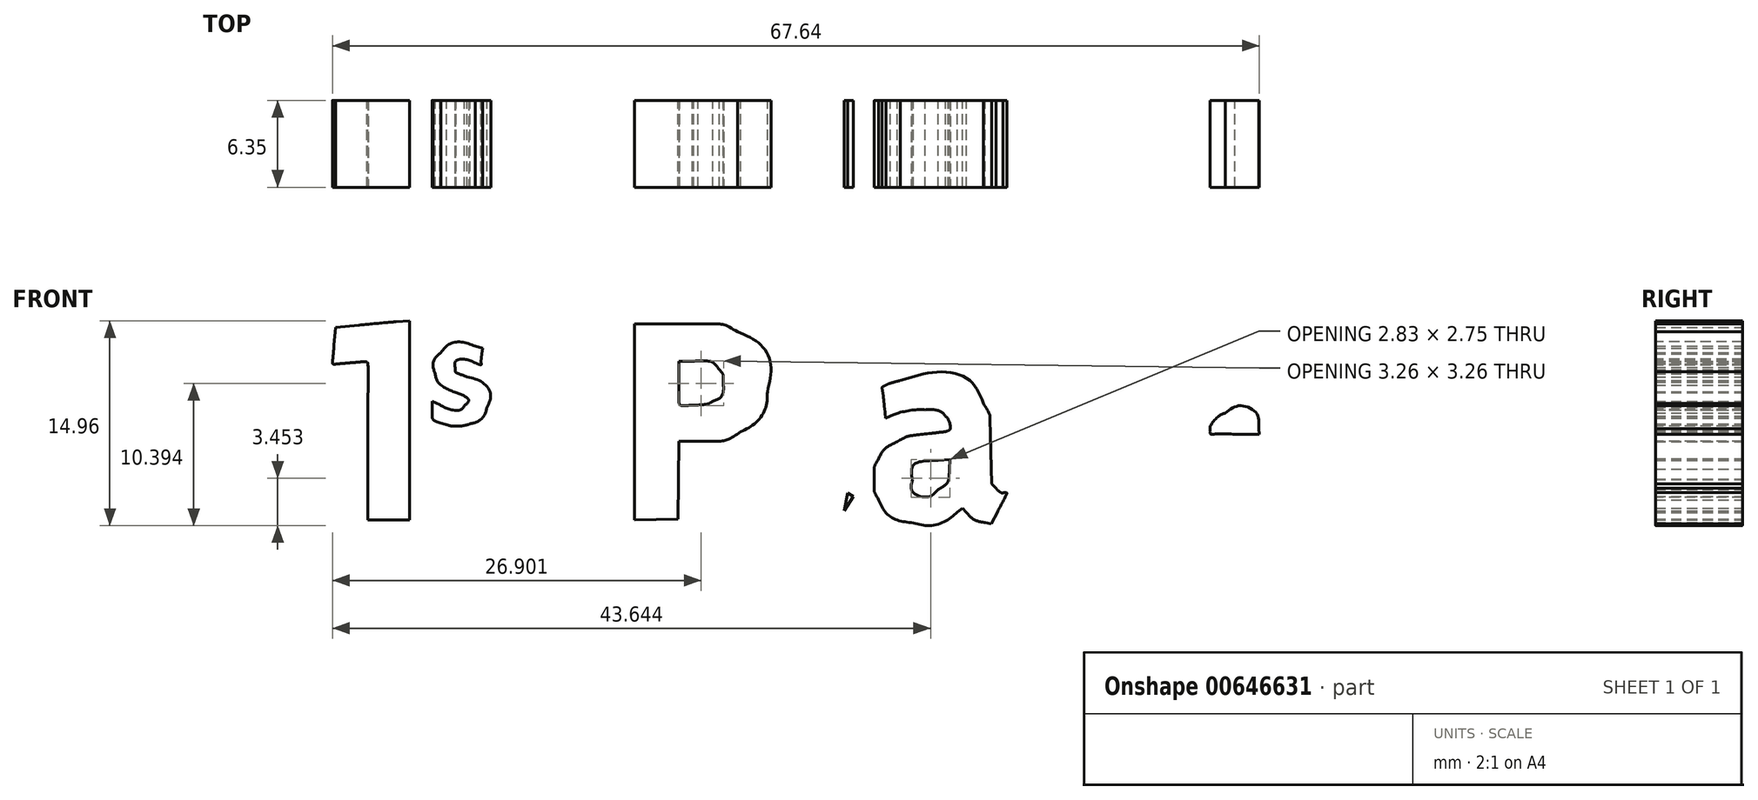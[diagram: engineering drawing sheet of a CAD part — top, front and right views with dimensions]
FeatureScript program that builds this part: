
annotation { "Feature Type Name" : "Feature", "Feature Type Description" : "" }
export const myFeature = defineFeature(function(context is Context, id is Id, definition is map)
    precondition{}
    {
        {
            var Q0;
            Q0=qCreatedBy(makeId("Front.planeOp"),FACE);
            var sketch = newSketch(context, id + "F0", { "sketchPlane" : qUnion([Q0])});
            skFitSpline(sketch, "E0", {"points": [v(0.33, -8.9) * mm, v(-0.3, -8.66) * mm, v(-0.98, -8.12) * mm, v(-1.33, -7.57) * mm]});
            skFitSpline(sketch, "E1", {"points": [v(-1.33, -7.57) * mm, v(-1.97, -6.57) * mm, v(-1.96, -6.72) * mm, v(-1.96, 0.66) * mm]});
            skFitSpline(sketch, "E2", {"points": [v(1.12, 0.8) * mm, v(1.12, -6.54) * mm, v(1.08, -6.16) * mm, v(1.9, -6.65) * mm]});
            skFitSpline(sketch, "E3", {"points": [v(1.64, -7.94) * mm, v(1.27, -8.51) * mm, v(0.9, -9) * mm, v(0.84, -9) * mm]});
            skFitSpline(sketch, "E4", {"points": [v(0.84, -9) * mm, v(0.76, -9.02) * mm, v(0.54, -8.97) * mm, v(0.33, -8.9) * mm]});
            skLineSegment(sketch, "E5", {"start": v(1.9, -6.65) * mm, "end": v(2.3, -6.9) * mm});
            skLineSegment(sketch, "E6", {"start": v(2.3, -6.9) * mm, "end": v(1.64, -7.94) * mm});
            skLineSegment(sketch, "E7", {"start": v(1.64, -7.94) * mm, "end": v(1.9, -6.65) * mm});
            skFitSpline(sketch, "E8", {"points": [v(6.68, -8.82) * mm, v(5.5, -8.61) * mm, v(4.66, -8.05) * mm, v(4.15, -7.14) * mm]});
            skFitSpline(sketch, "E9", {"points": [v(4.15, -7.14) * mm, v(3.87, -6.63) * mm, v(3.84, -6.48) * mm, v(3.84, -5.63) * mm]});
            skFitSpline(sketch, "E10", {"points": [v(3.84, -5.63) * mm, v(3.84, -4.8) * mm, v(3.87, -4.64) * mm, v(4.15, -4.14) * mm]});
            skFitSpline(sketch, "E11", {"points": [v(4.15, -4.14) * mm, v(4.46, -3.57) * mm, v(4.8, -3.26) * mm, v(5.51, -2.9) * mm]});
            skFitSpline(sketch, "E12", {"points": [v(5.51, -2.9) * mm, v(6.22, -2.53) * mm, v(6.51, -2.45) * mm, v(7.83, -2.3) * mm]});
            skFitSpline(sketch, "E13", {"points": [v(7.83, -2.3) * mm, v(8.53, -2.22) * mm, v(9.16, -2.12) * mm, v(9.22, -2.08) * mm]});
            skFitSpline(sketch, "E14", {"points": [v(9.22, -2.08) * mm, v(9.38, -1.99) * mm, v(9.25, -1.3) * mm, v(9.03, -1.05) * mm]});
            skFitSpline(sketch, "E15", {"points": [v(9.03, -1.05) * mm, v(8.76, -0.73) * mm, v(8.24, -0.56) * mm, v(7.55, -0.56) * mm]});
            skFitSpline(sketch, "E16", {"points": [v(7.55, -0.56) * mm, v(6.85, -0.56) * mm, v(5.57, -0.8) * mm, v(5, -1.03) * mm]});
            skFitSpline(sketch, "E17", {"points": [v(4.58, -0.43) * mm, v(4.54, -0.01) * mm, v(4.49, 0.5) * mm, v(4.46, 0.71) * mm]});
            skFitSpline(sketch, "E18", {"points": [v(4.46, 0.71) * mm, v(4.4, 1.05) * mm, v(4.43, 1.11) * mm, v(4.7, 1.25) * mm]});
            skFitSpline(sketch, "E19", {"points": [v(4.7, 1.25) * mm, v(4.86, 1.33) * mm, v(5.33, 1.47) * mm, v(5.75, 1.57) * mm]});
            skFitSpline(sketch, "E20", {"points": [v(5.75, 1.57) * mm, v(8.56, 2.2) * mm, v(10.81, 1.58) * mm, v(11.8, -0.1) * mm]});
            skFitSpline(sketch, "E21", {"points": [v(11.8, -0.1) * mm, v(12.23, -0.83) * mm, v(12.28, -1.14) * mm, v(12.35, -3.61) * mm]});
            skLineSegment(sketch, "E22", {"start": v(5, -1.03) * mm, "end": v(4.65, -1.18) * mm});
            skLineSegment(sketch, "E23", {"start": v(4.65, -1.18) * mm, "end": v(4.58, -0.43) * mm});
            skFitSpline(sketch, "E24", {"points": [v(12.72, -6.3) * mm, v(12.9, -6.48) * mm, v(13.12, -6.63) * mm, v(13.23, -6.63) * mm]});
            skFitSpline(sketch, "E25", {"points": [v(13.23, -6.63) * mm, v(13.5, -6.63) * mm, v(13.43, -6.86) * mm, v(12.84, -8) * mm]});
            skLineSegment(sketch, "E26", {"start": v(12.35, -3.61) * mm, "end": v(12.42, -5.99) * mm});
            skLineSegment(sketch, "E27", {"start": v(12.42, -5.99) * mm, "end": v(12.72, -6.3) * mm});
            skFitSpline(sketch, "E28", {"points": [v(11.93, -8.8) * mm, v(11.35, -8.68) * mm, v(10.92, -8.44) * mm, v(10.58, -8.06) * mm]});
            skLineSegment(sketch, "E29", {"start": v(12.84, -8) * mm, "end": v(12.36, -8.9) * mm});
            skLineSegment(sketch, "E30", {"start": v(12.36, -8.9) * mm, "end": v(11.93, -8.8) * mm});
            skFitSpline(sketch, "E31", {"points": [v(9.91, -8.03) * mm, v(9, -8.72) * mm, v(7.78, -9.02) * mm, v(6.68, -8.82) * mm]});
            skLineSegment(sketch, "E32", {"start": v(10.58, -8.06) * mm, "end": v(10.28, -7.74) * mm});
            skLineSegment(sketch, "E33", {"start": v(10.28, -7.74) * mm, "end": v(9.91, -8.03) * mm});
            skFitSpline(sketch, "E34", {"points": [v(8.5, -6.4) * mm, v(9.08, -6) * mm, v(9.26, -5.65) * mm, v(9.31, -4.88) * mm]});
            skFitSpline(sketch, "E35", {"points": [v(8.49, -4.26) * mm, v(7.1, -4.38) * mm, v(6.61, -4.74) * mm, v(6.61, -5.67) * mm]});
            skFitSpline(sketch, "E36", {"points": [v(6.61, -5.67) * mm, v(6.61, -6.52) * mm, v(7.7, -6.93) * mm, v(8.5, -6.4) * mm]});
            skLineSegment(sketch, "E37", {"start": v(9.31, -4.88) * mm, "end": v(9.36, -4.2) * mm});
            skLineSegment(sketch, "E38", {"start": v(9.36, -4.2) * mm, "end": v(8.49, -4.26) * mm});
            skFitSpline(sketch, "E39", {"points": [v(19.3, -8.81) * mm, v(18.14, -8.62) * mm, v(16.94, -7.97) * mm, v(16.1, -7.07) * mm]});
            skFitSpline(sketch, "E40", {"points": [v(16.1, -7.07) * mm, v(14.63, -5.48) * mm, v(14.33, -3.05) * mm, v(15.38, -1.04) * mm]});
            skFitSpline(sketch, "E41", {"points": [v(15.38, -1.04) * mm, v(16.6, 1.31) * mm, v(19.52, 2.37) * mm, v(22.46, 1.53) * mm]});
            skFitSpline(sketch, "E42", {"points": [v(22.46, 1.53) * mm, v(23.5, 1.23) * mm, v(23.5, 1.24) * mm, v(23.37, -0.19) * mm]});
            skFitSpline(sketch, "E43", {"points": [v(23.37, -0.19) * mm, v(23.32, -0.85) * mm, v(23.25, -1.42) * mm, v(23.22, -1.45) * mm]});
            skFitSpline(sketch, "E44", {"points": [v(23.22, -1.45) * mm, v(23.19, -1.48) * mm, v(22.93, -1.4) * mm, v(22.65, -1.28) * mm]});
            skFitSpline(sketch, "E45", {"points": [v(22.65, -1.28) * mm, v(22.28, -1.11) * mm, v(21.87, -1.03) * mm, v(21.17, -1) * mm]});
            skFitSpline(sketch, "E46", {"points": [v(21.17, -1) * mm, v(19.85, -0.94) * mm, v(19.36, -1.09) * mm, v(18.68, -1.76) * mm]});
            skFitSpline(sketch, "E47", {"points": [v(18.68, -1.76) * mm, v(18.21, -2.21) * mm, v(18.12, -2.38) * mm, v(18.01, -2.9) * mm]});
            skFitSpline(sketch, "E48", {"points": [v(18.01, -2.9) * mm, v(17.8, -3.92) * mm, v(18, -4.62) * mm, v(18.7, -5.28) * mm]});
            skFitSpline(sketch, "E49", {"points": [v(18.7, -5.28) * mm, v(19.43, -5.97) * mm, v(19.69, -6.05) * mm, v(21.1, -6.05) * mm]});
            skFitSpline(sketch, "E50", {"points": [v(21.1, -6.05) * mm, v(22.17, -6.05) * mm, v(22.42, -6.02) * mm, v(22.86, -5.82) * mm]});
            skFitSpline(sketch, "E51", {"points": [v(23.3, -6.44) * mm, v(23.26, -6.92) * mm, v(23.2, -7.55) * mm, v(23.17, -7.85) * mm]});
            skLineSegment(sketch, "E52", {"start": v(22.86, -5.82) * mm, "end": v(23.37, -5.58) * mm});
            skLineSegment(sketch, "E53", {"start": v(23.37, -5.58) * mm, "end": v(23.3, -6.44) * mm});
            skFitSpline(sketch, "E54", {"points": [v(22.54, -8.56) * mm, v(21.5, -8.9) * mm, v(20.31, -8.98) * mm, v(19.3, -8.81) * mm]});
            skLineSegment(sketch, "E55", {"start": v(23.17, -7.85) * mm, "end": v(23.1, -8.38) * mm});
            skLineSegment(sketch, "E56", {"start": v(23.1, -8.38) * mm, "end": v(22.54, -8.56) * mm});
            skFitSpline(sketch, "E57", {"points": [v(29.9, -8.83) * mm, v(27, -8.3) * mm, v(25.12, -6.2) * mm, v(25.12, -3.5) * mm]});
            skFitSpline(sketch, "E58", {"points": [v(25.12, -3.5) * mm, v(25.12, -1.07) * mm, v(26.47, 0.82) * mm, v(28.78, 1.6) * mm]});
            skFitSpline(sketch, "E59", {"points": [v(28.78, 1.6) * mm, v(29.57, 1.86) * mm, v(31.13, 1.86) * mm, v(31.91, 1.59) * mm]});
            skFitSpline(sketch, "E60", {"points": [v(31.91, 1.59) * mm, v(32.98, 1.22) * mm, v(33.71, 0.67) * mm, v(34.26, -0.2) * mm]});
            skFitSpline(sketch, "E61", {"points": [v(34.26, -0.2) * mm, v(34.7, -0.87) * mm, v(34.84, -1.41) * mm, v(34.84, -2.28) * mm]});
            skFitSpline(sketch, "E62", {"points": [v(30.9, -4.43) * mm, v(28.12, -4.43) * mm, v(28.18, -4.42) * mm, v(28.5, -5.04) * mm]});
            skFitSpline(sketch, "E63", {"points": [v(28.5, -5.04) * mm, v(29.26, -6.48) * mm, v(31.57, -6.94) * mm, v(33.7, -6.07) * mm]});
            skLineSegment(sketch, "E64", {"start": v(34.84, -2.28) * mm, "end": v(34.84, -2.99) * mm});
            skLineSegment(sketch, "E65", {"start": v(34.84, -2.99) * mm, "end": v(34.15, -3.7) * mm});
            skLineSegment(sketch, "E66", {"start": v(34.15, -3.7) * mm, "end": v(33.45, -4.43) * mm});
            skLineSegment(sketch, "E67", {"start": v(33.45, -4.43) * mm, "end": v(30.9, -4.43) * mm});
            skFitSpline(sketch, "E68", {"points": [v(34.14, -7.04) * mm, v(34.06, -7.7) * mm, v(33.96, -8.28) * mm, v(33.9, -8.34) * mm]});
            skFitSpline(sketch, "E69", {"points": [v(33.9, -8.34) * mm, v(33.55, -8.7) * mm, v(30.94, -9.02) * mm, v(29.9, -8.83) * mm]});
            skLineSegment(sketch, "E70", {"start": v(33.7, -6.07) * mm, "end": v(34.28, -5.83) * mm});
            skLineSegment(sketch, "E71", {"start": v(34.28, -5.83) * mm, "end": v(34.14, -7.04) * mm});
            skFitSpline(sketch, "E72", {"points": [v(31.89, -1.93) * mm, v(31.74, -0.84) * mm, v(30.51, -0.27) * mm, v(29.46, -0.8) * mm]});
            skFitSpline(sketch, "E73", {"points": [v(29.46, -0.8) * mm, v(28.95, -1.05) * mm, v(28.36, -1.8) * mm, v(28.36, -2.18) * mm]});
            skFitSpline(sketch, "E74", {"points": [v(28.36, -2.18) * mm, v(28.36, -2.32) * mm, v(28.6, -2.34) * mm, v(30.15, -2.34) * mm]});
            skLineSegment(sketch, "E75", {"start": v(29.9, -8.83) * mm, "end": v(29.9, -8.83) * mm});
            skFitSpline(sketch, "E76", {"points": [v(-33.12, -2.87) * mm, v(-33.12, 0.29) * mm, v(-33.15, 2.9) * mm, v(-33.2, 2.92) * mm]});
            skFitSpline(sketch, "E77", {"points": [v(-33.2, 2.92) * mm, v(-33.24, 2.95) * mm, v(-33.8, 2.92) * mm, v(-34.46, 2.86) * mm]});
            skFitSpline(sketch, "E78", {"points": [v(-34.46, 2.86) * mm, v(-35.1, 2.8) * mm, v(-35.66, 2.78) * mm, v(-35.67, 2.8) * mm]});
            skFitSpline(sketch, "E79", {"points": [v(-35.67, 2.8) * mm, v(-35.7, 2.82) * mm, v(-35.65, 3.42) * mm, v(-35.59, 4.14) * mm]});
            skLineSegment(sketch, "E80", {"start": v(30.15, -2.34) * mm, "end": v(31.94, -2.34) * mm});
            skLineSegment(sketch, "E81", {"start": v(31.94, -2.34) * mm, "end": v(31.89, -1.93) * mm});
            skFitSpline(sketch, "E82", {"points": [v(-33.75, 5.62) * mm, v(-32.8, 5.72) * mm, v(-31.59, 5.83) * mm, v(-31.05, 5.87) * mm]});
            skLineSegment(sketch, "E83", {"start": v(-35.59, 4.14) * mm, "end": v(-35.47, 5.45) * mm});
            skLineSegment(sketch, "E84", {"start": v(-35.47, 5.45) * mm, "end": v(-33.75, 5.62) * mm});
            skLineSegment(sketch, "E85", {"start": v(-31.05, 5.87) * mm, "end": v(-30.09, 5.94) * mm});
            skLineSegment(sketch, "E86", {"start": v(-30.09, 5.94) * mm, "end": v(-30.09, -1.33) * mm});
            skLineSegment(sketch, "E87", {"start": v(-30.09, -1.33) * mm, "end": v(-30.09, -8.61) * mm});
            skLineSegment(sketch, "E88", {"start": v(-30.09, -8.61) * mm, "end": v(-31.6, -8.61) * mm});
            skLineSegment(sketch, "E89", {"start": v(-31.6, -8.61) * mm, "end": v(-33.12, -8.61) * mm});
            skLineSegment(sketch, "E90", {"start": v(-33.12, -8.61) * mm, "end": v(-33.12, -2.87) * mm});
            skFitSpline(sketch, "E91", {"points": [v(-10.82, 5.7) * mm, v(-7.69, 5.7) * mm, v(-7.06, 5.63) * mm, v(-6.15, 5.13) * mm]});
            skFitSpline(sketch, "E92", {"points": [v(-6.15, 5.13) * mm, v(-4.48, 4.22) * mm, v(-3.73, 2.7) * mm, v(-3.96, 0.75) * mm]});
            skFitSpline(sketch, "E93", {"points": [v(-3.96, 0.75) * mm, v(-4.1, -0.45) * mm, v(-4.81, -1.5) * mm, v(-5.92, -2.17) * mm]});
            skFitSpline(sketch, "E94", {"points": [v(-5.92, -2.17) * mm, v(-6.84, -2.73) * mm, v(-7.45, -2.86) * mm, v(-9.04, -2.86) * mm]});
            skLineSegment(sketch, "E95", {"start": v(-13.67, -1.45) * mm, "end": v(-13.67, 5.71) * mm});
            skLineSegment(sketch, "E96", {"start": v(-13.67, 5.71) * mm, "end": v(-10.82, 5.7) * mm});
            skFitSpline(sketch, "E97", {"points": [v(-7.95, 0.05) * mm, v(-7.4, 0.33) * mm, v(-7.19, 0.72) * mm, v(-7.19, 1.46) * mm]});
            skFitSpline(sketch, "E98", {"points": [v(-7.19, 1.46) * mm, v(-7.19, 1.93) * mm, v(-7.24, 2.1) * mm, v(-7.47, 2.37) * mm]});
            skFitSpline(sketch, "E99", {"points": [v(-7.47, 2.37) * mm, v(-7.89, 2.86) * mm, v(-8.3, 3) * mm, v(-9.43, 3) * mm]});
            skLineSegment(sketch, "E100", {"start": v(-9.04, -2.86) * mm, "end": v(-10.43, -2.86) * mm});
            skLineSegment(sketch, "E101", {"start": v(-10.43, -2.86) * mm, "end": v(-10.45, -5.71) * mm});
            skLineSegment(sketch, "E102", {"start": v(-10.45, -5.71) * mm, "end": v(-10.48, -8.56) * mm});
            skLineSegment(sketch, "E103", {"start": v(-10.48, -8.56) * mm, "end": v(-12.08, -8.6) * mm});
            skLineSegment(sketch, "E104", {"start": v(-12.08, -8.6) * mm, "end": v(-13.67, -8.62) * mm});
            skLineSegment(sketch, "E105", {"start": v(-13.67, -8.62) * mm, "end": v(-13.67, -1.45) * mm});
            skFitSpline(sketch, "E106", {"points": [v(-10.43, 1.44) * mm, v(-10.43, 0.59) * mm, v(-10.4, -0.15) * mm, v(-10.35, -0.2) * mm]});
            skFitSpline(sketch, "E107", {"points": [v(-10.35, -0.2) * mm, v(-10.3, -0.24) * mm, v(-9.85, -0.25) * mm, v(-9.33, -0.22) * mm]});
            skFitSpline(sketch, "E108", {"points": [v(-9.33, -0.22) * mm, v(-8.65, -0.19) * mm, v(-8.27, -0.12) * mm, v(-7.95, 0.05) * mm]});
            skLineSegment(sketch, "E109", {"start": v(-9.43, 3) * mm, "end": v(-10.43, 3) * mm});
            skLineSegment(sketch, "E110", {"start": v(-10.43, 3) * mm, "end": v(-10.43, 1.44) * mm});
            skFitSpline(sketch, "E111", {"points": [v(-27.37, -1.65) * mm, v(-28.29, -1.35) * mm, v(-28.4, -1.2) * mm, v(-28.41, -0.39) * mm]});
            skFitSpline(sketch, "E112", {"points": [v(-27.86, -0.2) * mm, v(-27.17, -0.53) * mm, v(-26.33, -0.55) * mm, v(-26.07, -0.26) * mm]});
            skFitSpline(sketch, "E113", {"points": [v(-26.07, -0.26) * mm, v(-25.77, 0.08) * mm, v(-25.95, 0.36) * mm, v(-26.68, 0.69) * mm]});
            skFitSpline(sketch, "E114", {"points": [v(-26.68, 0.69) * mm, v(-27.55, 1.08) * mm, v(-28.07, 1.55) * mm, v(-28.2, 2.06) * mm]});
            skFitSpline(sketch, "E115", {"points": [v(-28.2, 2.06) * mm, v(-28.37, 2.67) * mm, v(-28.24, 3.17) * mm, v(-27.8, 3.6) * mm]});
            skFitSpline(sketch, "E116", {"points": [v(-27.8, 3.6) * mm, v(-27.17, 4.23) * mm, v(-26.32, 4.4) * mm, v(-25.28, 4.08) * mm]});
            skLineSegment(sketch, "E117", {"start": v(-28.41, -0.39) * mm, "end": v(-28.41, 0.05) * mm});
            skLineSegment(sketch, "E118", {"start": v(-28.41, 0.05) * mm, "end": v(-27.86, -0.2) * mm});
            skFitSpline(sketch, "E119", {"points": [v(-24.8, 3.53) * mm, v(-24.83, 3.32) * mm, v(-24.86, 3.05) * mm, v(-24.86, 2.93) * mm]});
            skFitSpline(sketch, "E120", {"points": [v(-24.86, 2.93) * mm, v(-24.86, 2.71) * mm, v(-24.88, 2.7) * mm, v(-25.25, 2.84) * mm]});
            skFitSpline(sketch, "E121", {"points": [v(-25.25, 2.84) * mm, v(-26.04, 3.13) * mm, v(-26.74, 2.98) * mm, v(-26.74, 2.53) * mm]});
            skFitSpline(sketch, "E122", {"points": [v(-26.74, 2.53) * mm, v(-26.74, 2.22) * mm, v(-26.61, 2.12) * mm, v(-25.88, 1.84) * mm]});
            skFitSpline(sketch, "E123", {"points": [v(-25.88, 1.84) * mm, v(-24.72, 1.41) * mm, v(-24.16, 0.54) * mm, v(-24.44, -0.38) * mm]});
            skFitSpline(sketch, "E124", {"points": [v(-24.44, -0.38) * mm, v(-24.6, -0.92) * mm, v(-25.1, -1.42) * mm, v(-25.67, -1.59) * mm]});
            skFitSpline(sketch, "E125", {"points": [v(-25.67, -1.59) * mm, v(-26.08, -1.71) * mm, v(-27.06, -1.75) * mm, v(-27.37, -1.65) * mm]});
            skLineSegment(sketch, "E126", {"start": v(-25.28, 4.08) * mm, "end": v(-24.73, 3.92) * mm});
            skLineSegment(sketch, "E127", {"start": v(-24.73, 3.92) * mm, "end": v(-24.8, 3.53) * mm});
            skFitSpline(sketch, "E128", {"points": [v(-21.57, -1.44) * mm, v(-21.95, -1.23) * mm, v(-22.33, -0.9) * mm, v(-22.49, -0.62) * mm]});
            skFitSpline(sketch, "E129", {"points": [v(-22.49, -0.62) * mm, v(-22.56, -0.5) * mm, v(-22.63, 0.25) * mm, v(-22.66, 1.1) * mm]});
            skFitSpline(sketch, "E130", {"points": [v(-21.89, 5.5) * mm, v(-21.5, 5.67) * mm, v(-21.13, 5.78) * mm, v(-21.07, 5.75) * mm]});
            skFitSpline(sketch, "E131", {"points": [v(-21.07, 5.75) * mm, v(-21.02, 5.72) * mm, v(-21, 5.33) * mm, v(-21, 4.89) * mm]});
            skLineSegment(sketch, "E132", {"start": v(-22.66, 1.1) * mm, "end": v(-22.72, 2.63) * mm});
            skLineSegment(sketch, "E133", {"start": v(-22.72, 2.63) * mm, "end": v(-23.21, 2.66) * mm});
            skLineSegment(sketch, "E134", {"start": v(-23.21, 2.66) * mm, "end": v(-23.7, 2.69) * mm});
            skLineSegment(sketch, "E135", {"start": v(-23.7, 2.69) * mm, "end": v(-23.7, 3.36) * mm});
            skLineSegment(sketch, "E136", {"start": v(-23.7, 3.36) * mm, "end": v(-23.7, 4.03) * mm});
            skLineSegment(sketch, "E137", {"start": v(-23.7, 4.03) * mm, "end": v(-23.21, 4.06) * mm});
            skLineSegment(sketch, "E138", {"start": v(-23.21, 4.06) * mm, "end": v(-22.72, 4.09) * mm});
            skLineSegment(sketch, "E139", {"start": v(-22.72, 4.09) * mm, "end": v(-22.66, 4.65) * mm});
            skLineSegment(sketch, "E140", {"start": v(-22.66, 4.65) * mm, "end": v(-22.61, 5.2) * mm});
            skLineSegment(sketch, "E141", {"start": v(-22.61, 5.2) * mm, "end": v(-21.89, 5.5) * mm});
            skFitSpline(sketch, "E142", {"points": [v(-19.29, 3.48) * mm, v(-19.36, 2.65) * mm, v(-19.33, 2.68) * mm, v(-20.2, 2.68) * mm]});
            skLineSegment(sketch, "E143", {"start": v(-21, 4.89) * mm, "end": v(-21.04, 4.09) * mm});
            skLineSegment(sketch, "E144", {"start": v(-21.04, 4.09) * mm, "end": v(-20.14, 4.06) * mm});
            skLineSegment(sketch, "E145", {"start": v(-20.14, 4.06) * mm, "end": v(-19.24, 4.03) * mm});
            skLineSegment(sketch, "E146", {"start": v(-19.24, 4.03) * mm, "end": v(-19.29, 3.48) * mm});
            skFitSpline(sketch, "E147", {"points": [v(-21, 1.44) * mm, v(-21, -0.02) * mm, v(-20.93, -0.14) * mm, v(-20.21, -0.22) * mm]});
            skLineSegment(sketch, "E148", {"start": v(-20.2, 2.68) * mm, "end": v(-21, 2.68) * mm});
            skLineSegment(sketch, "E149", {"start": v(-21, 2.68) * mm, "end": v(-21, 1.44) * mm});
            skFitSpline(sketch, "E150", {"points": [v(-19.78, -0.85) * mm, v(-19.81, -1.17) * mm, v(-19.87, -1.47) * mm, v(-19.9, -1.52) * mm]});
            skFitSpline(sketch, "E151", {"points": [v(-19.9, -1.52) * mm, v(-20, -1.67) * mm, v(-21.23, -1.61) * mm, v(-21.57, -1.44) * mm]});
            skLineSegment(sketch, "E152", {"start": v(-20.21, -0.22) * mm, "end": v(-19.71, -0.28) * mm});
            skLineSegment(sketch, "E153", {"start": v(-19.71, -0.28) * mm, "end": v(-19.78, -0.85) * mm});
            skLineSegment(sketch, "E154", {"start": v(-1.96, 5.7) * mm, "end": v(1.12, 5.7) * mm});
            skLineSegment(sketch, "E155", {"start": v(1.12, 5.7) * mm, "end": v(1.12, 0.8) * mm});
            skLineSegment(sketch, "E156", {"start": v(-1.96, 5.7) * mm, "end": v(-1.96, 0.66) * mm});
            skSolve(sketch);
        }
        {
            var Q0;
            Q0 = qSketchRegion(id + "F0", true);
            extrude(context, id + "F1", {"entities" : qUnion([Q0]), "depth" : 6.35 * mm, "offsetDistance" : 25.4 * mm});
        }
    });
